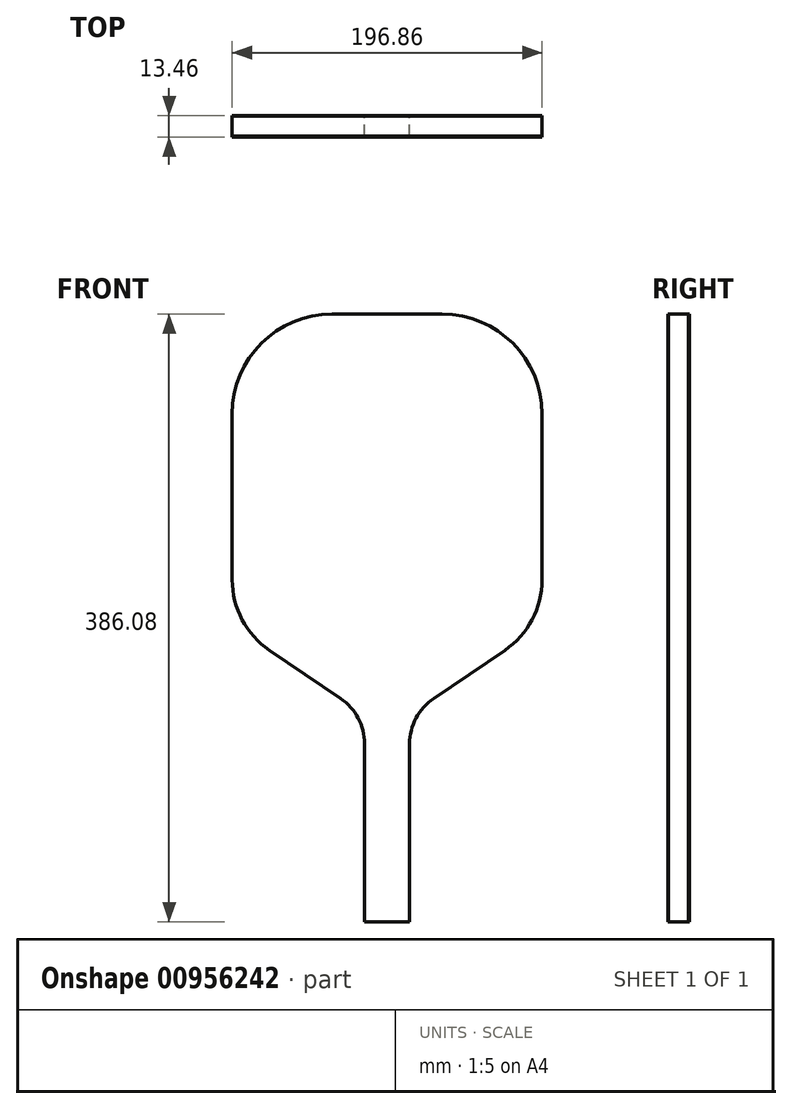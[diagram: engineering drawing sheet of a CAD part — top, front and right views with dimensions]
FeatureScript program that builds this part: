
annotation { "Feature Type Name" : "Feature", "Feature Type Description" : "" }
export const myFeature = defineFeature(function(context is Context, id is Id, definition is map)
    precondition{}
    {
        {
            var Q0;
            Q0=qCreatedBy(makeId("Front.planeOp"),FACE);
            var sketch = newSketch(context, id + "F0", { "sketchPlane" : qUnion([Q0])});
            skLineSegment(sketch, "E0", {"start": v(0, 0) * mm, "end": v(14.29, 0) * mm});
            skLineSegment(sketch, "E1", {"start": v(14.29, 0) * mm, "end": v(14.29, 113.03) * mm});
            skLineSegment(sketch, "E2", {"start": v(29.63, 141.95) * mm, "end": v(74.71, 172.48) * mm});
            skLineSegment(sketch, "E3", {"start": v(98.43, 217.17) * mm, "end": v(98.42, 322.58) * mm});
            skLineSegment(sketch, "E4", {"start": v(34.92, 386.08) * mm, "end": v(0, 386.08) * mm});
            skLineSegment(sketch, "E5", {"start": v(0, 386.08) * mm, "end": v(0, 0) * mm, "construction": true});
            skPoint(sketch, "E6.visualSharp", {"position": v(14.29, 131.56) * mm});
            skArc(sketch, "E6.filletArc", {"start": v(29.63, 141.95) * mm, "mid": v(18.36, 129.4) * mm, "end": v(14.29, 113.03) * mm});
            skPoint(sketch, "E7.visualSharp", {"position": v(14.29, 0) * mm});
            skPoint(sketch, "E8.visualSharp", {"position": v(98.43, 188.53) * mm});
            skArc(sketch, "E8.filletArc", {"start": v(74.71, 172.48) * mm, "mid": v(92.13, 191.87) * mm, "end": v(98.42, 217.17) * mm});
            skPoint(sketch, "E9.visualSharp", {"position": v(98.42, 386.08) * mm});
            skArc(sketch, "E9.filletArc", {"start": v(98.42, 322.58) * mm, "mid": v(79.83, 367.48) * mm, "end": v(34.92, 386.08) * mm});
            skLineSegment(sketch, "E10.MirrorCS", {"start": v(0, 0) * mm, "end": v(-14.29, 0) * mm});
            skLineSegment(sketch, "E11.MirrorCS", {"start": v(-14.29, 0) * mm, "end": v(-14.29, 113.03) * mm});
            skArc(sketch, "E12.MirrorCS", {"start": v(-29.63, 141.95) * mm, "mid": v(-18.36, 129.4) * mm, "end": v(-14.29, 113.03) * mm});
            skLineSegment(sketch, "E13.MirrorCS", {"start": v(-29.63, 141.95) * mm, "end": v(-74.71, 172.48) * mm});
            skArc(sketch, "E14.MirrorCS", {"start": v(-74.71, 172.48) * mm, "mid": v(-92.13, 191.87) * mm, "end": v(-98.43, 217.17) * mm});
            skLineSegment(sketch, "E15.MirrorCS", {"start": v(-98.43, 217.17) * mm, "end": v(-98.43, 322.58) * mm});
            skArc(sketch, "E16.MirrorCS", {"start": v(-98.43, 322.58) * mm, "mid": v(-79.83, 367.48) * mm, "end": v(-34.93, 386.08) * mm});
            skLineSegment(sketch, "E17.MirrorCS", {"start": v(-34.93, 386.08) * mm, "end": v(0, 386.08) * mm});
            skSolve(sketch);
        }
        {
            var Q0;
            Q0 = qSketchRegion(id + "F0", true);
            extrude(context, id + "F1", {"entities" : qUnion([Q0]), "depth" : 12.7 * mm, "offsetDistance" : 25.4 * mm});
        }
        {
            var Q0;
            Q0=makeQuery(id+"F1.opExtrude","CAP_FACE",FACE,{"disambiguationData":[OSD([sQuery(id+"F0.wireOp",EDGE,"E0"),sQuery(id+"F0.wireOp",EDGE,"E1"),sQuery(id+"F0.wireOp",EDGE,"E2"),sQuery(id+"F0.wireOp",EDGE,"E3"),sQuery(id+"F0.wireOp",EDGE,"E4"),sQuery(id+"F0.wireOp",EDGE,"E6.filletArc"),sQuery(id+"F0.wireOp",EDGE,"E8.filletArc"),sQuery(id+"F0.wireOp",EDGE,"E9.filletArc"),sQuery(id+"F0.wireOp",EDGE,"E10.MirrorCS"),sQuery(id+"F0.wireOp",EDGE,"E11.MirrorCS"),sQuery(id+"F0.wireOp",EDGE,"E12.MirrorCS"),sQuery(id+"F0.wireOp",EDGE,"E13.MirrorCS"),sQuery(id+"F0.wireOp",EDGE,"E14.MirrorCS"),sQuery(id+"F0.wireOp",EDGE,"E15.MirrorCS"),sQuery(id+"F0.wireOp",EDGE,"E16.MirrorCS"),sQuery(id+"F0.wireOp",EDGE,"E17.MirrorCS")])],"isStart":false});
            var sketch = newSketch(context, id + "F2", { "sketchPlane" : qUnion([Q0])});
            skLineSegment(sketch, "E18.0", {"start": v(14.29, 0) * mm, "end": v(-14.29, 0) * mm});
            skLineSegment(sketch, "E18.1", {"start": v(14.29, 0) * mm, "end": v(14.29, 113.03) * mm});
            skLineSegment(sketch, "E18.2", {"start": v(-14.29, 0) * mm, "end": v(-14.29, 113.03) * mm});
            skArc(sketch, "E18.3", {"start": v(29.63, 141.95) * mm, "mid": v(18.36, 129.4) * mm, "end": v(14.29, 113.03) * mm});
            skLineSegment(sketch, "E18.4", {"start": v(29.63, 141.95) * mm, "end": v(74.71, 172.48) * mm});
            skArc(sketch, "E18.5", {"start": v(74.71, 172.48) * mm, "mid": v(92.13, 191.87) * mm, "end": v(98.42, 217.17) * mm});
            skLineSegment(sketch, "E18.6", {"start": v(98.43, 217.17) * mm, "end": v(98.42, 322.58) * mm});
            skArc(sketch, "E18.7", {"start": v(98.42, 322.58) * mm, "mid": v(79.83, 367.48) * mm, "end": v(34.92, 386.08) * mm});
            skLineSegment(sketch, "E18.8", {"start": v(34.92, 386.08) * mm, "end": v(-34.93, 386.08) * mm});
            skArc(sketch, "E18.9", {"start": v(-98.43, 322.58) * mm, "mid": v(-79.83, 367.48) * mm, "end": v(-34.93, 386.08) * mm});
            skLineSegment(sketch, "E18.10", {"start": v(-98.43, 217.17) * mm, "end": v(-98.43, 322.58) * mm});
            skArc(sketch, "E18.11", {"start": v(-74.71, 172.48) * mm, "mid": v(-92.13, 191.87) * mm, "end": v(-98.43, 217.17) * mm});
            skLineSegment(sketch, "E18.12", {"start": v(-29.63, 141.95) * mm, "end": v(-74.71, 172.48) * mm});
            skArc(sketch, "E18.13", {"start": v(-29.63, 141.95) * mm, "mid": v(-18.36, 129.4) * mm, "end": v(-14.29, 113.03) * mm});
            skSolve(sketch);
        }
        {
            var Q0;
            Q0 = qSketchRegion(id + "F2", true);
            extrude(context, id + "F3", {"entities" : qUnion([Q0]), "depth" : 0.38 * mm, "offsetDistance" : 25.4 * mm});
        }
        {
            var Q0;
            Q0=makeQuery(id+"F1.opExtrude","CAP_FACE",FACE,{"disambiguationData":[OSD([sQuery(id+"F0.wireOp",EDGE,"E0"),sQuery(id+"F0.wireOp",EDGE,"E1"),sQuery(id+"F0.wireOp",EDGE,"E2"),sQuery(id+"F0.wireOp",EDGE,"E3"),sQuery(id+"F0.wireOp",EDGE,"E4"),sQuery(id+"F0.wireOp",EDGE,"E6.filletArc"),sQuery(id+"F0.wireOp",EDGE,"E8.filletArc"),sQuery(id+"F0.wireOp",EDGE,"E9.filletArc"),sQuery(id+"F0.wireOp",EDGE,"E10.MirrorCS"),sQuery(id+"F0.wireOp",EDGE,"E11.MirrorCS"),sQuery(id+"F0.wireOp",EDGE,"E12.MirrorCS"),sQuery(id+"F0.wireOp",EDGE,"E13.MirrorCS"),sQuery(id+"F0.wireOp",EDGE,"E14.MirrorCS"),sQuery(id+"F0.wireOp",EDGE,"E15.MirrorCS"),sQuery(id+"F0.wireOp",EDGE,"E16.MirrorCS"),sQuery(id+"F0.wireOp",EDGE,"E17.MirrorCS")])],"isStart":true});
            var sketch = newSketch(context, id + "F4", { "sketchPlane" : qUnion([Q0])});
            skLineSegment(sketch, "E19.0", {"start": v(-14.29, 0) * mm, "end": v(14.29, 0) * mm});
            skLineSegment(sketch, "E19.1", {"start": v(14.29, 0) * mm, "end": v(14.29, 113.03) * mm});
            skArc(sketch, "E19.2", {"start": v(29.63, 141.95) * mm, "mid": v(18.36, 129.4) * mm, "end": v(14.29, 113.03) * mm});
            skLineSegment(sketch, "E19.3", {"start": v(29.63, 141.95) * mm, "end": v(74.71, 172.48) * mm});
            skLineSegment(sketch, "E19.4", {"start": v(-14.29, 0) * mm, "end": v(-14.29, 113.03) * mm});
            skArc(sketch, "E19.5", {"start": v(-29.63, 141.95) * mm, "mid": v(-18.36, 129.4) * mm, "end": v(-14.29, 113.03) * mm});
            skLineSegment(sketch, "E19.6", {"start": v(-29.63, 141.95) * mm, "end": v(-74.71, 172.48) * mm});
            skArc(sketch, "E19.7", {"start": v(74.71, 172.48) * mm, "mid": v(92.13, 191.87) * mm, "end": v(98.43, 217.17) * mm});
            skLineSegment(sketch, "E19.8", {"start": v(98.43, 217.17) * mm, "end": v(98.43, 322.58) * mm});
            skArc(sketch, "E19.9", {"start": v(98.43, 322.58) * mm, "mid": v(79.83, 367.48) * mm, "end": v(34.93, 386.08) * mm});
            skLineSegment(sketch, "E19.10", {"start": v(-34.92, 386.08) * mm, "end": v(34.93, 386.08) * mm});
            skArc(sketch, "E19.11", {"start": v(-98.42, 322.58) * mm, "mid": v(-79.83, 367.48) * mm, "end": v(-34.92, 386.08) * mm});
            skLineSegment(sketch, "E19.12", {"start": v(-98.43, 217.17) * mm, "end": v(-98.42, 322.58) * mm});
            skArc(sketch, "E19.13", {"start": v(-74.71, 172.48) * mm, "mid": v(-92.13, 191.87) * mm, "end": v(-98.42, 217.17) * mm});
            skPoint(sketch, "E19.14", {"position": v(92.13, 191.87) * mm});
            skPoint(sketch, "E19.15", {"position": v(79.83, 367.48) * mm});
            skPoint(sketch, "E19.16", {"position": v(-92.13, 191.87) * mm});
            skSolve(sketch);
        }
        {
            var Q0;
            Q0 = qSketchRegion(id + "F4", true);
            extrude(context, id + "F5", {"entities" : qUnion([Q0]), "depth" : 0.38 * mm, "offsetDistance" : 25.4 * mm});
        }
    });
